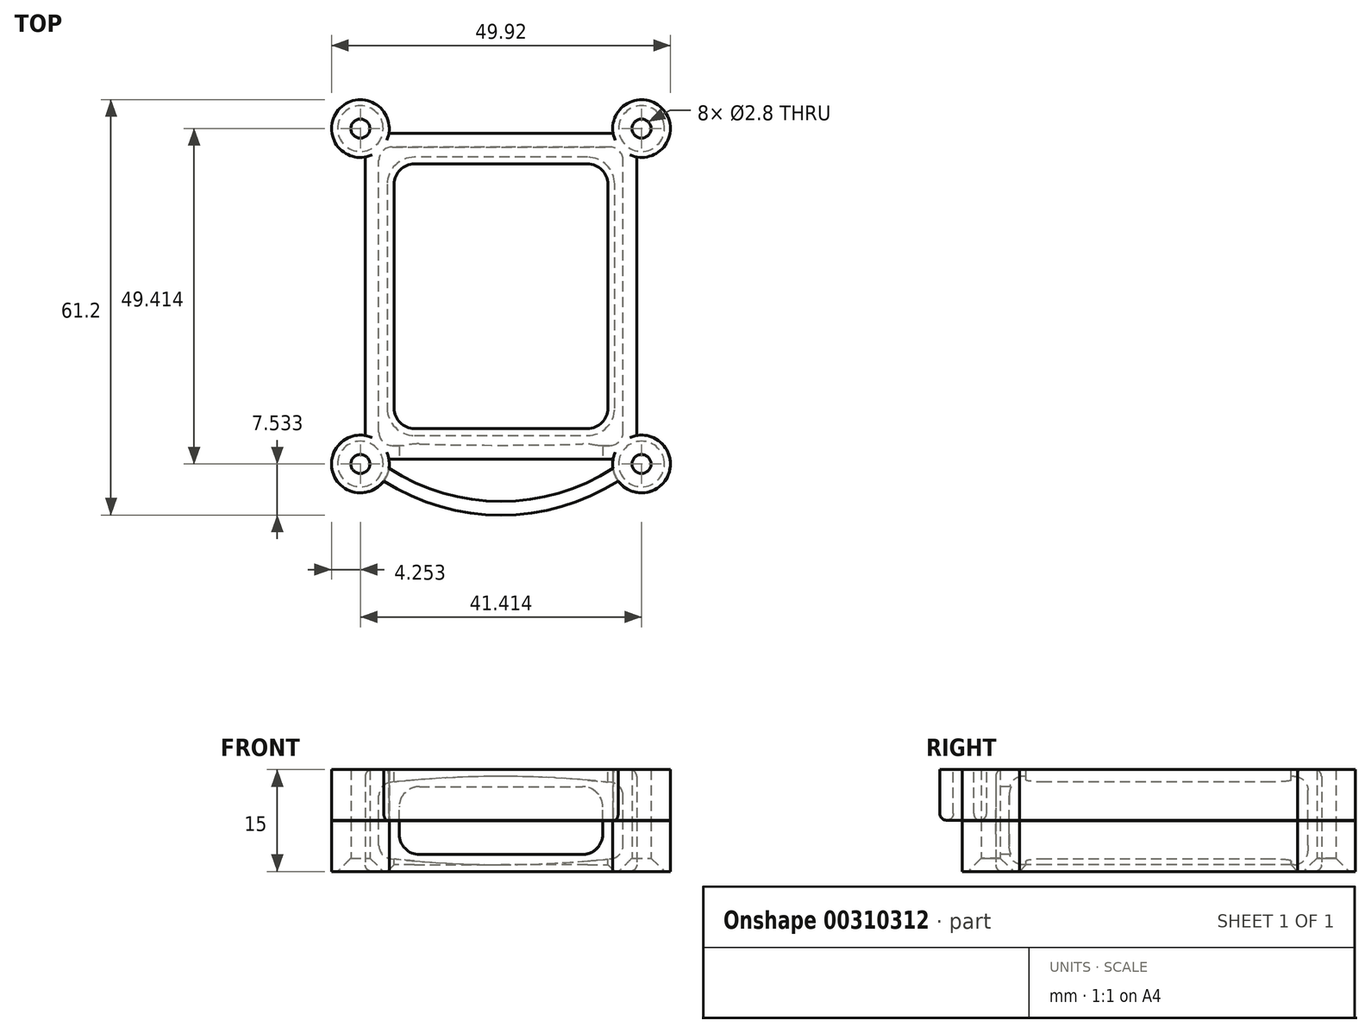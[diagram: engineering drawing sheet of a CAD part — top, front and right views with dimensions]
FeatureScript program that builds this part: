
annotation { "Feature Type Name" : "Feature", "Feature Type Description" : "" }
export const myFeature = defineFeature(function(context is Context, id is Id, definition is map)
    precondition{}
    {
        {
            var Q0;
            Q0=qCreatedBy(makeId("Top.planeOp"),FACE);
            var sketch = newSketch(context, id + "F0", { "sketchPlane" : qUnion([Q0])});
            skLineSegment(sketch, "E0.bottom", {"start": v(20, 24) * mm, "end": v(-20, 24) * mm});
            skLineSegment(sketch, "E0.top", {"start": v(20, -24) * mm, "end": v(-20, -24) * mm});
            skLineSegment(sketch, "E0.left", {"start": v(20, 24) * mm, "end": v(20, -24) * mm});
            skLineSegment(sketch, "E0.right", {"start": v(-20, 24) * mm, "end": v(-20, -24) * mm});
            skPoint(sketch, "E0.middle", {"position": v(0, 0) * mm});
            skSolve(sketch);
        }
        {
            var Q0;
            Q0 = qSketchRegion(id + "F0", true);
            extrude(context, id + "F1", {"entities" : qUnion([Q0]), "endBound" : BoundingType.SYMMETRIC, "depth" : 15 * mm});
        }
        {
            var Q0;
            Q0=qCreatedBy(makeId("Front.planeOp"),FACE);
            var sketch = newSketch(context, id + "F2", { "sketchPlane" : qUnion([Q0])});
            skLineSegment(sketch, "E1.bottom", {"start": v(18, -6.5) * mm, "end": v(-18, -6.5) * mm, "construction": true});
            skLineSegment(sketch, "E1.top", {"start": v(18, 6.5) * mm, "end": v(-18, 6.5) * mm, "construction": true});
            skLineSegment(sketch, "E1.left", {"start": v(18, -6.5) * mm, "end": v(18, 6.5) * mm, "construction": true});
            skLineSegment(sketch, "E1.right", {"start": v(-18, -6.5) * mm, "end": v(-18, 6.5) * mm, "construction": true});
            skPoint(sketch, "E1.middle", {"position": v(0, 0) * mm});
            skArc(sketch, "E2", {"start": v(-18, 5.42) * mm, "mid": v(0, 6.5) * mm, "end": v(18, 5.42) * mm});
            skArc(sketch, "E3.MirrorCS", {"start": v(-18, -5.42) * mm, "mid": v(0, -6.5) * mm, "end": v(18, -5.42) * mm});
            skLineSegment(sketch, "E4", {"start": v(-18, 5.42) * mm, "end": v(-18, -5.42) * mm});
            skLineSegment(sketch, "E5", {"start": v(18, 5.42) * mm, "end": v(18, -5.42) * mm});
            skSolve(sketch);
        }
        {
            var Q0;
            Q0 = qSketchRegion(id + "F2", true);
            extrude(context, id + "F3", {"entities" : qUnion([Q0]), "operationType" : NewBodyOperationType.REMOVE, "endBound" : BoundingType.SYMMETRIC, "oppositeDirection" : true, "depth" : 44 * mm});
        }
        {
            var Q0;
            Q0=makeQuery(id+"F3.boolean.opBoolean","COPY",EDGE,{"derivedFrom":makeQuery(id+"F3.opExtrude","CAP_EDGE",EDGE,{"disambiguationData":[OSD([sQuery(id+"F2.wireOp",EDGE,"E4")])],"isStart":true})});
            var Q1;
            Q1=makeQuery(id+"F3.boolean.opBoolean","COPY",EDGE,{"derivedFrom":makeQuery(id+"F3.opExtrude","CAP_EDGE",EDGE,{"disambiguationData":[OSD([sQuery(id+"F2.wireOp",EDGE,"E4")])],"isStart":false})});
            var Q2;
            Q2=makeQuery(id+"F3.boolean.opBoolean","COPY",EDGE,{"derivedFrom":makeQuery(id+"F3.opExtrude","CAP_EDGE",EDGE,{"disambiguationData":[OSD([sQuery(id+"F2.wireOp",EDGE,"E5")])],"isStart":false})});
            var Q3;
            Q3=makeQuery(id+"F3.boolean.opBoolean","COPY",EDGE,{"derivedFrom":makeQuery(id+"F3.opExtrude","CAP_EDGE",EDGE,{"disambiguationData":[OSD([sQuery(id+"F2.wireOp",EDGE,"E5")])],"isStart":true})});
            var Q4;
            Q4=makeQuery(id+"F3.boolean.opBoolean","COPY",EDGE,{"derivedFrom":makeQuery(id+"F3.opExtrude","SWEPT_EDGE",EDGE,{"disambiguationData":[OSD([sQuery(id+"F2.wireOp",EDGE,"E2"),sQuery(id+"F2.wireOp",EDGE,"E4")])]})});
            var Q5;
            Q5=makeQuery(id+"F3.boolean.opBoolean","COPY",EDGE,{"derivedFrom":makeQuery(id+"F3.opExtrude","SWEPT_EDGE",EDGE,{"disambiguationData":[OSD([sQuery(id+"F2.wireOp",EDGE,"E3.MirrorCS"),sQuery(id+"F2.wireOp",EDGE,"E4")])]})});
            var Q6;
            Q6=makeQuery(id+"F3.boolean.opBoolean","COPY",EDGE,{"derivedFrom":makeQuery(id+"F3.opExtrude","SWEPT_EDGE",EDGE,{"disambiguationData":[OSD([sQuery(id+"F2.wireOp",EDGE,"E3.MirrorCS"),sQuery(id+"F2.wireOp",EDGE,"E5")])]})});
            var Q7;
            Q7=makeQuery(id+"F3.boolean.opBoolean","COPY",EDGE,{"derivedFrom":makeQuery(id+"F3.opExtrude","SWEPT_EDGE",EDGE,{"disambiguationData":[OSD([sQuery(id+"F2.wireOp",EDGE,"E2"),sQuery(id+"F2.wireOp",EDGE,"E5")])]})});
            var Q8;
            Q8=makeQuery(id+"F3.boolean.opBoolean","COPY",EDGE,{"derivedFrom":makeQuery(id+"F3.opExtrude","CAP_EDGE",EDGE,{"disambiguationData":[OSD([sQuery(id+"F2.wireOp",EDGE,"E3.MirrorCS")])],"isStart":false})});
            var Q9;
            Q9=makeQuery(id+"F3.boolean.opBoolean","COPY",EDGE,{"derivedFrom":makeQuery(id+"F3.opExtrude","CAP_EDGE",EDGE,{"disambiguationData":[OSD([sQuery(id+"F2.wireOp",EDGE,"E2")])],"isStart":false})});
            var Q10;
            Q10=makeQuery(id+"F3.boolean.opBoolean","COPY",EDGE,{"derivedFrom":makeQuery(id+"F3.opExtrude","CAP_EDGE",EDGE,{"disambiguationData":[OSD([sQuery(id+"F2.wireOp",EDGE,"E2")])],"isStart":true})});
            var Q11;
            Q11=makeQuery(id+"F3.boolean.opBoolean","COPY",EDGE,{"derivedFrom":makeQuery(id+"F3.opExtrude","CAP_EDGE",EDGE,{"disambiguationData":[OSD([sQuery(id+"F2.wireOp",EDGE,"E3.MirrorCS")])],"isStart":true})});
            fillet(context, id + "F4", {"entities" : qUnion([Q0, Q1, Q2, Q3, Q4, Q5, Q6, Q7, Q8, Q9, Q10, Q11]), "radius" : 2 * mm, "tangentPropagation" : true, "allowEdgeOverflow" : false});
        }
        {
            var Q0;
            Q0=makeQuery(id+"F1.opExtrude","CAP_FACE",FACE,{"disambiguationData":[OSD([sQuery(id+"F0.wireOp",EDGE,"E0.bottom"),sQuery(id+"F0.wireOp",EDGE,"E0.top"),sQuery(id+"F0.wireOp",EDGE,"E0.left"),sQuery(id+"F0.wireOp",EDGE,"E0.right")])],"isStart":false});
            var sketch = newSketch(context, id + "F5", { "sketchPlane" : qUnion([Q0])});
            skLineSegment(sketch, "E6", {"start": v(20, 24) * mm, "end": v(20.7, 24.7) * mm, "construction": true});
            skCircle(sketch, "E7", {"center": v(20.7, 24.7) * mm, "radius": 4.25 * mm});
            skLineSegment(sketch, "E8", {"start": v(20, -24) * mm, "end": v(20.7, -24.7) * mm, "construction": true});
            skLineSegment(sketch, "E9", {"start": v(-20, -24) * mm, "end": v(-20.7, -24.7) * mm, "construction": true});
            skLineSegment(sketch, "E10", {"start": v(-20, 24) * mm, "end": v(-20.7, 24.7) * mm, "construction": true});
            skCircle(sketch, "E11", {"center": v(-20.7, 24.7) * mm, "radius": 4.25 * mm});
            skCircle(sketch, "E12", {"center": v(-20.7, -24.7) * mm, "radius": 4.25 * mm});
            skCircle(sketch, "E13", {"center": v(20.7, -24.7) * mm, "radius": 4.25 * mm});
            skSolve(sketch);
        }
        {
            var Q0;
            Q0 = qSketchRegion(id + "F5", true);
            var Q1;
            Q1=makeQuery(id+"F1.opExtrude","CAP_FACE",FACE,{"disambiguationData":[OSD([sQuery(id+"F0.wireOp",EDGE,"E0.bottom"),sQuery(id+"F0.wireOp",EDGE,"E0.top"),sQuery(id+"F0.wireOp",EDGE,"E0.left"),sQuery(id+"F0.wireOp",EDGE,"E0.right")])],"isStart":true});
            extrude(context, id + "F6", {"entities" : qUnion([Q0]), "operationType" : NewBodyOperationType.ADD, "endBound" : BoundingType.UP_TO_SURFACE, "oppositeDirection" : true, "endBoundEntityFace" : qUnion([Q1]), "depth" : 25 * mm});
        }
        {
            var Q0;
            Q0=makeQuery(id+"F6.boolean.opBoolean","MERGE",FACE,{"derivedFrom":[makeQuery(id+"F1.opExtrude","CAP_FACE",FACE,{"disambiguationData":[OSD([sQuery(id+"F0.wireOp",EDGE,"E0.bottom"),sQuery(id+"F0.wireOp",EDGE,"E0.top"),sQuery(id+"F0.wireOp",EDGE,"E0.left"),sQuery(id+"F0.wireOp",EDGE,"E0.right")])],"isStart":true}),makeQuery(id+"F6.opExtrude","CAP_FACE",FACE,{"disambiguationData":[OSD([sQuery(id+"F5.wireOp",EDGE,"E7")])],"isStart":false}),makeQuery(id+"F6.opExtrude","CAP_FACE",FACE,{"disambiguationData":[OSD([sQuery(id+"F5.wireOp",EDGE,"E11")])],"isStart":false}),makeQuery(id+"F6.opExtrude","CAP_FACE",FACE,{"disambiguationData":[OSD([sQuery(id+"F5.wireOp",EDGE,"E12")])],"isStart":false}),makeQuery(id+"F6.opExtrude","CAP_FACE",FACE,{"disambiguationData":[OSD([sQuery(id+"F5.wireOp",EDGE,"E13")])],"isStart":false})]});
            var sketch = newSketch(context, id + "F7", { "sketchPlane" : qUnion([Q0])});
            skArc(sketch, "E14", {"start": v(-20.7, 24.7) * mm, "mid": v(0, 32.24) * mm, "end": v(20.7, 24.7) * mm, "construction": true});
            skArc(sketch, "E15.0", {"start": v(-19.42, 23.17) * mm, "mid": v(0, 30.24) * mm, "end": v(19.42, 23.17) * mm, "construction": true});
            skArc(sketch, "E16", {"start": v(17.28, 27.22) * mm, "mid": v(0, 32.24) * mm, "end": v(-17.28, 27.22) * mm});
            skArc(sketch, "E17", {"start": v(16.5, 25.34) * mm, "mid": v(0, 30.24) * mm, "end": v(-16.5, 25.34) * mm});
            skLineSegment(sketch, "E18", {"start": v(-17.28, 27.22) * mm, "end": v(-16.5, 25.34) * mm});
            skLineSegment(sketch, "E19", {"start": v(17.28, 27.22) * mm, "end": v(16.5, 25.34) * mm});
            skSolve(sketch);
        }
        {
            var Q0;
            Q0=makeQuery(id+"F6.boolean.opBoolean","MERGE",FACE,{"derivedFrom":[makeQuery(id+"F1.opExtrude","CAP_FACE",FACE,{"disambiguationData":[OSD([sQuery(id+"F0.wireOp",EDGE,"E0.bottom"),sQuery(id+"F0.wireOp",EDGE,"E0.top"),sQuery(id+"F0.wireOp",EDGE,"E0.left"),sQuery(id+"F0.wireOp",EDGE,"E0.right")])],"isStart":false}),makeQuery(id+"F6.opExtrude","CAP_FACE",FACE,{"disambiguationData":[OSD([sQuery(id+"F5.wireOp",EDGE,"E7")])],"isStart":true}),makeQuery(id+"F6.opExtrude","CAP_FACE",FACE,{"disambiguationData":[OSD([sQuery(id+"F5.wireOp",EDGE,"E11")])],"isStart":true}),makeQuery(id+"F6.opExtrude","CAP_FACE",FACE,{"disambiguationData":[OSD([sQuery(id+"F5.wireOp",EDGE,"E12")])],"isStart":true}),makeQuery(id+"F6.opExtrude","CAP_FACE",FACE,{"disambiguationData":[OSD([sQuery(id+"F5.wireOp",EDGE,"E13")])],"isStart":true})]});
            var sketch = newSketch(context, id + "F8", { "sketchPlane" : qUnion([Q0])});
            skPoint(sketch, "E20.0", {"position": v(-20.7, 24.7) * mm});
            skPoint(sketch, "E20.1", {"position": v(20.7, 24.7) * mm});
            skPoint(sketch, "E20.2", {"position": v(-20.7, -24.7) * mm});
            skPoint(sketch, "E20.3", {"position": v(20.7, -24.7) * mm});
            skSolve(sketch);
        }
        {
            var Q0;
            Q0=sQuery(id+"F8.wireOp",VERTEX,"E20.0");
            var Q1;
            Q1=sQuery(id+"F8.wireOp",VERTEX,"E20.1");
            var Q2;
            Q2=sQuery(id+"F8.wireOp",VERTEX,"E20.2");
            var Q3;
            Q3=sQuery(id+"F8.wireOp",VERTEX,"E20.3");
            var Q4;
            Q4=makeQuery(id+"F1.opExtrude","SWEPT_BODY",BODY,{"disambiguationData":[OSD([sQuery(id+"F0.wireOp",EDGE,"E0.bottom"),sQuery(id+"F0.wireOp",EDGE,"E0.top"),sQuery(id+"F0.wireOp",EDGE,"E0.left"),sQuery(id+"F0.wireOp",EDGE,"E0.right")])]});
            hole(context, id + "F9", {"style" : HoleStyle.C_SINK, "endStyle" : HoleEndStyle.THROUGH, "standardTappedOrClearance" : lookupTablePath({ "standard" : "ISO", "size" : "2.8", "type" : "Drilled" }), "standardBlindInLast" : lookupTablePath({ "standard" : "ISO", "size" : "2.8", "type" : "Drilled" }), "holeDiameter" : 2.8 * mm, "cSinkDiameter" : 6.72 * mm, "cSinkAngle" : 90 * degree, "tappedDepth" : 12 * mm, "tapClearance" : 3, "locations" : qUnion([Q0, Q1, Q2, Q3]), "scope" : qUnion([Q4])});
        }
        {
            var Q0;
            Q0=qCreatedBy(makeId("Front.planeOp"),FACE);
            var sketch = newSketch(context, id + "F10", { "sketchPlane" : qUnion([Q0])});
            skLineSegment(sketch, "E21.bottom", {"start": v(27.5, 0.05) * mm, "end": v(-27.5, 0.05) * mm});
            skLineSegment(sketch, "E21.top", {"start": v(27.5, -0.05) * mm, "end": v(-27.5, -0.05) * mm});
            skLineSegment(sketch, "E21.left", {"start": v(27.5, 0.05) * mm, "end": v(27.5, -0.05) * mm});
            skLineSegment(sketch, "E21.right", {"start": v(-27.5, 0.05) * mm, "end": v(-27.5, -0.05) * mm});
            skPoint(sketch, "E21.middle", {"position": v(0, 0) * mm});
            skSolve(sketch);
        }
        {
            var Q0;
            Q0 = qSketchRegion(id + "F10", true);
            extrude(context, id + "F11", {"entities" : qUnion([Q0]), "operationType" : NewBodyOperationType.REMOVE, "endBound" : BoundingType.SYMMETRIC, "oppositeDirection" : true, "depth" : 60 * mm});
        }
        {
            var Q0;
            Q0=qCreatedBy(makeId("Top.planeOp"),FACE);
            var sketch = newSketch(context, id + "F12", { "sketchPlane" : qUnion([Q0])});
            skLineSegment(sketch, "E22.bottom", {"start": v(12.75, 19.5) * mm, "end": v(-12.75, 19.5) * mm});
            skLineSegment(sketch, "E22.top", {"start": v(12.75, -19.5) * mm, "end": v(-12.75, -19.5) * mm});
            skLineSegment(sketch, "E22.left", {"start": v(15.75, 16.5) * mm, "end": v(15.75, -16.5) * mm});
            skLineSegment(sketch, "E22.right", {"start": v(-15.75, 16.5) * mm, "end": v(-15.75, -16.5) * mm});
            skPoint(sketch, "E22.middle", {"position": v(0, 0) * mm});
            skPoint(sketch, "E23.visualSharp", {"position": v(-15.75, 19.5) * mm});
            skArc(sketch, "E23.filletArc", {"start": v(-12.75, 19.5) * mm, "mid": v(-14.87, 18.62) * mm, "end": v(-15.75, 16.5) * mm});
            skPoint(sketch, "E24.visualSharp", {"position": v(15.75, 19.5) * mm});
            skArc(sketch, "E24.filletArc", {"start": v(15.75, 16.5) * mm, "mid": v(14.87, 18.62) * mm, "end": v(12.75, 19.5) * mm});
            skPoint(sketch, "E25.visualSharp", {"position": v(-15.75, -19.5) * mm});
            skArc(sketch, "E25.filletArc", {"start": v(-15.75, -16.5) * mm, "mid": v(-14.87, -18.62) * mm, "end": v(-12.75, -19.5) * mm});
            skPoint(sketch, "E26.visualSharp", {"position": v(15.75, -19.5) * mm});
            skArc(sketch, "E26.filletArc", {"start": v(12.75, -19.5) * mm, "mid": v(14.87, -18.62) * mm, "end": v(15.75, -16.5) * mm});
            skSolve(sketch);
        }
        {
            var Q0;
            Q0 = qSketchRegion(id + "F12", true);
            extrude(context, id + "F13", {"entities" : qUnion([Q0]), "operationType" : NewBodyOperationType.REMOVE, "endBound" : BoundingType.SYMMETRIC, "depth" : 25 * mm});
        }
        {
            var Q0;
            Q0=makeQuery(id+"F1.opExtrude","CAP_EDGE",EDGE,{"disambiguationData":[OSD([sQuery(id+"F0.wireOp",EDGE,"E0.top")])],"isStart":false});
            var Q1;
            Q1=makeQuery(id+"F1.opExtrude","CAP_EDGE",EDGE,{"disambiguationData":[OSD([sQuery(id+"F0.wireOp",EDGE,"E0.left")])],"isStart":false});
            var Q2;
            Q2=makeQuery(id+"F1.opExtrude","CAP_EDGE",EDGE,{"disambiguationData":[OSD([sQuery(id+"F0.wireOp",EDGE,"E0.bottom")])],"isStart":false});
            var Q3;
            Q3=makeQuery(id+"F1.opExtrude","CAP_EDGE",EDGE,{"disambiguationData":[OSD([sQuery(id+"F0.wireOp",EDGE,"E0.right")])],"isStart":false});
            var Q4;
            Q4=makeQuery(id+"F1.opExtrude","CAP_EDGE",EDGE,{"disambiguationData":[OSD([sQuery(id+"F0.wireOp",EDGE,"E0.top")])],"isStart":true});
            var Q5;
            Q5=makeQuery(id+"F1.opExtrude","CAP_EDGE",EDGE,{"disambiguationData":[OSD([sQuery(id+"F0.wireOp",EDGE,"E0.right")])],"isStart":true});
            var Q6;
            Q6=makeQuery(id+"F1.opExtrude","CAP_EDGE",EDGE,{"disambiguationData":[OSD([sQuery(id+"F0.wireOp",EDGE,"E0.bottom")])],"isStart":true});
            var Q7;
            Q7=makeQuery(id+"F1.opExtrude","CAP_EDGE",EDGE,{"disambiguationData":[OSD([sQuery(id+"F0.wireOp",EDGE,"E0.left")])],"isStart":true});
            fillet(context, id + "F14", {"entities" : qUnion([Q0, Q1, Q2, Q3, Q4, Q5, Q6, Q7]), "radius" : 1 * mm, "tangentPropagation" : true, "allowEdgeOverflow" : false});
        }
        {
            var Q0;
            {var subQ1=sQuery(id+"F0.wireOp",EDGE,"E0.top");Q0=makeQuery(id+"F11.boolean.opBoolean","SPLIT",FACE,{"disambiguationData":[TD([makeQuery(id+"F6.opExtrude","CAP_FACE",FACE,{"disambiguationData":[OSD([sQuery(id+"F5.wireOp",EDGE,"E7")])],"isStart":true})])],"derivedFrom":makeQuery(id+"F1.opExtrude","SWEPT_FACE",FACE,{"disambiguationData":[OSD([subQ1])]})});}
            var sketch = newSketch(context, id + "F15", { "sketchPlane" : qUnion([Q0])});
            skLineSegment(sketch, "E27.bottom", {"start": v(12, 5) * mm, "end": v(-12, 5) * mm});
            skLineSegment(sketch, "E27.top", {"start": v(12, -5) * mm, "end": v(-12, -5) * mm});
            skLineSegment(sketch, "E27.left", {"start": v(15, 2) * mm, "end": v(15, -2) * mm});
            skLineSegment(sketch, "E27.right", {"start": v(-15, 2) * mm, "end": v(-15, -2) * mm});
            skPoint(sketch, "E27.middle", {"position": v(0, 0) * mm});
            skPoint(sketch, "E28.visualSharp", {"position": v(-15, 5) * mm});
            skArc(sketch, "E28.filletArc", {"start": v(-12, 5) * mm, "mid": v(-14.12, 4.12) * mm, "end": v(-15, 2) * mm});
            skPoint(sketch, "E29.visualSharp", {"position": v(15, 5) * mm});
            skArc(sketch, "E29.filletArc", {"start": v(15, 2) * mm, "mid": v(14.12, 4.12) * mm, "end": v(12, 5) * mm});
            skPoint(sketch, "E30.visualSharp", {"position": v(15, -5) * mm});
            skArc(sketch, "E30.filletArc", {"start": v(12, -5) * mm, "mid": v(14.12, -4.12) * mm, "end": v(15, -2) * mm});
            skPoint(sketch, "E31.visualSharp", {"position": v(-15, -5) * mm});
            skArc(sketch, "E31.filletArc", {"start": v(-15, -2) * mm, "mid": v(-14.12, -4.12) * mm, "end": v(-12, -5) * mm});
            skSolve(sketch);
        }
        {
            var Q0;
            Q0 = qSketchRegion(id + "F15", true);
            extrude(context, id + "F16", {"entities" : qUnion([Q0]), "operationType" : NewBodyOperationType.REMOVE, "oppositeDirection" : true, "depth" : 25 * mm});
        }
        {
            var Q0;
            Q0=makeQuery(id+"F13.boolean.opBoolean","INTERSECT",EDGE,{"derivedFrom":[makeQuery(id+"F6.boolean.opBoolean","MERGE",FACE,{"derivedFrom":[makeQuery(id+"F1.opExtrude","CAP_FACE",FACE,{"disambiguationData":[OSD([sQuery(id+"F0.wireOp",EDGE,"E0.bottom"),sQuery(id+"F0.wireOp",EDGE,"E0.top"),sQuery(id+"F0.wireOp",EDGE,"E0.left"),sQuery(id+"F0.wireOp",EDGE,"E0.right")])],"isStart":false}),makeQuery(id+"F6.opExtrude","CAP_FACE",FACE,{"disambiguationData":[OSD([sQuery(id+"F5.wireOp",EDGE,"E7")])],"isStart":true}),makeQuery(id+"F6.opExtrude","CAP_FACE",FACE,{"disambiguationData":[OSD([sQuery(id+"F5.wireOp",EDGE,"E11")])],"isStart":true}),makeQuery(id+"F6.opExtrude","CAP_FACE",FACE,{"disambiguationData":[OSD([sQuery(id+"F5.wireOp",EDGE,"E12")])],"isStart":true}),makeQuery(id+"F6.opExtrude","CAP_FACE",FACE,{"disambiguationData":[OSD([sQuery(id+"F5.wireOp",EDGE,"E13")])],"isStart":true})]}),makeQuery(id+"F13.opExtrude","SWEPT_FACE",FACE,{"disambiguationData":[OSD([sQuery(id+"F12.wireOp",EDGE,"E22.bottom")])]})]});
            chamfer(context, id + "F17", {"entities" : qUnion([Q0]), "width" : 1 * mm, "tangentPropagation" : true});
        }
        {
            var Q0;
            Q0 = qSketchRegion(id + "F7", true);
            var Q1;
            Q1=makeQuery(id+"F11.boolean.opBoolean","COPY",FACE,{"derivedFrom":makeQuery(id+"F11.opExtrude","SWEPT_FACE",FACE,{"disambiguationData":[OSD([sQuery(id+"F10.wireOp",EDGE,"E21.top")])]})});
            extrude(context, id + "F18", {"entities" : qUnion([Q0]), "operationType" : NewBodyOperationType.ADD, "endBound" : BoundingType.UP_TO_SURFACE, "oppositeDirection" : true, "endBoundEntityFace" : qUnion([Q1]), "depth" : 3 * mm, "offsetDistance" : 25 * mm});
        }
        {
            var Q0;
            Q0=makeQuery(id+"F18.opExtrude","CAP_EDGE",EDGE,{"disambiguationData":[OSD([sQuery(id+"F7.wireOp",EDGE,"E16")])],"isStart":false});
            var Q1;
            Q1=makeQuery(id+"F18.opExtrude","CAP_EDGE",EDGE,{"disambiguationData":[OSD([sQuery(id+"F7.wireOp",EDGE,"E17")])],"isStart":false});
            fillet(context, id + "F19", {"entities" : qUnion([Q0, Q1]), "radius" : 1 * mm, "tangentPropagation" : true, "allowEdgeOverflow" : false});
        }
        {
            var Q0;
            Q0=makeQuery(id+"F11.boolean.opBoolean","SPLIT",BODY,{"disambiguationData":[OD(0.0)],"derivedFrom":makeQuery(id+"F1.opExtrude","SWEPT_BODY",BODY,{"disambiguationData":[OSD([sQuery(id+"F0.wireOp",EDGE,"E0.bottom"),sQuery(id+"F0.wireOp",EDGE,"E0.top"),sQuery(id+"F0.wireOp",EDGE,"E0.left"),sQuery(id+"F0.wireOp",EDGE,"E0.right")])]})});
            var Q1;
            {var subQ1=sQuery(id+"F0.wireOp",EDGE,"E0.right");Q1=makeQuery(id+"F14.opFillet","BLEND_EDGE",EDGE,{"blendedFrom":[makeQuery(id+"F1.opExtrude","CAP_EDGE",EDGE,{"disambiguationData":[OSD([subQ1])],"isStart":false}),makeQuery(id+"F11.boolean.opBoolean","SPLIT",FACE,{"disambiguationData":[TD([makeQuery(id+"F6.opExtrude","CAP_FACE",FACE,{"disambiguationData":[OSD([sQuery(id+"F5.wireOp",EDGE,"E7")])],"isStart":true})])],"derivedFrom":makeQuery(id+"F1.opExtrude","SWEPT_FACE",FACE,{"disambiguationData":[OSD([subQ1])]})})],"blendedInto":[makeQuery(id+"F11.boolean.opBoolean","SPLIT",FACE,{"disambiguationData":[TD([makeQuery(id+"F6.opExtrude","CAP_FACE",FACE,{"disambiguationData":[OSD([sQuery(id+"F5.wireOp",EDGE,"E7")])],"isStart":true})])],"derivedFrom":makeQuery(id+"F1.opExtrude","SWEPT_FACE",FACE,{"disambiguationData":[OSD([subQ1])]})})]});}
            transform(context, id + "F20", {"entities" : qUnion([Q0]), "transformType" : TransformType.ROTATION, "transformAxis" : qUnion([Q1]), "angle" : 180 * degree, "makeCopy" : false});
        }
    });
